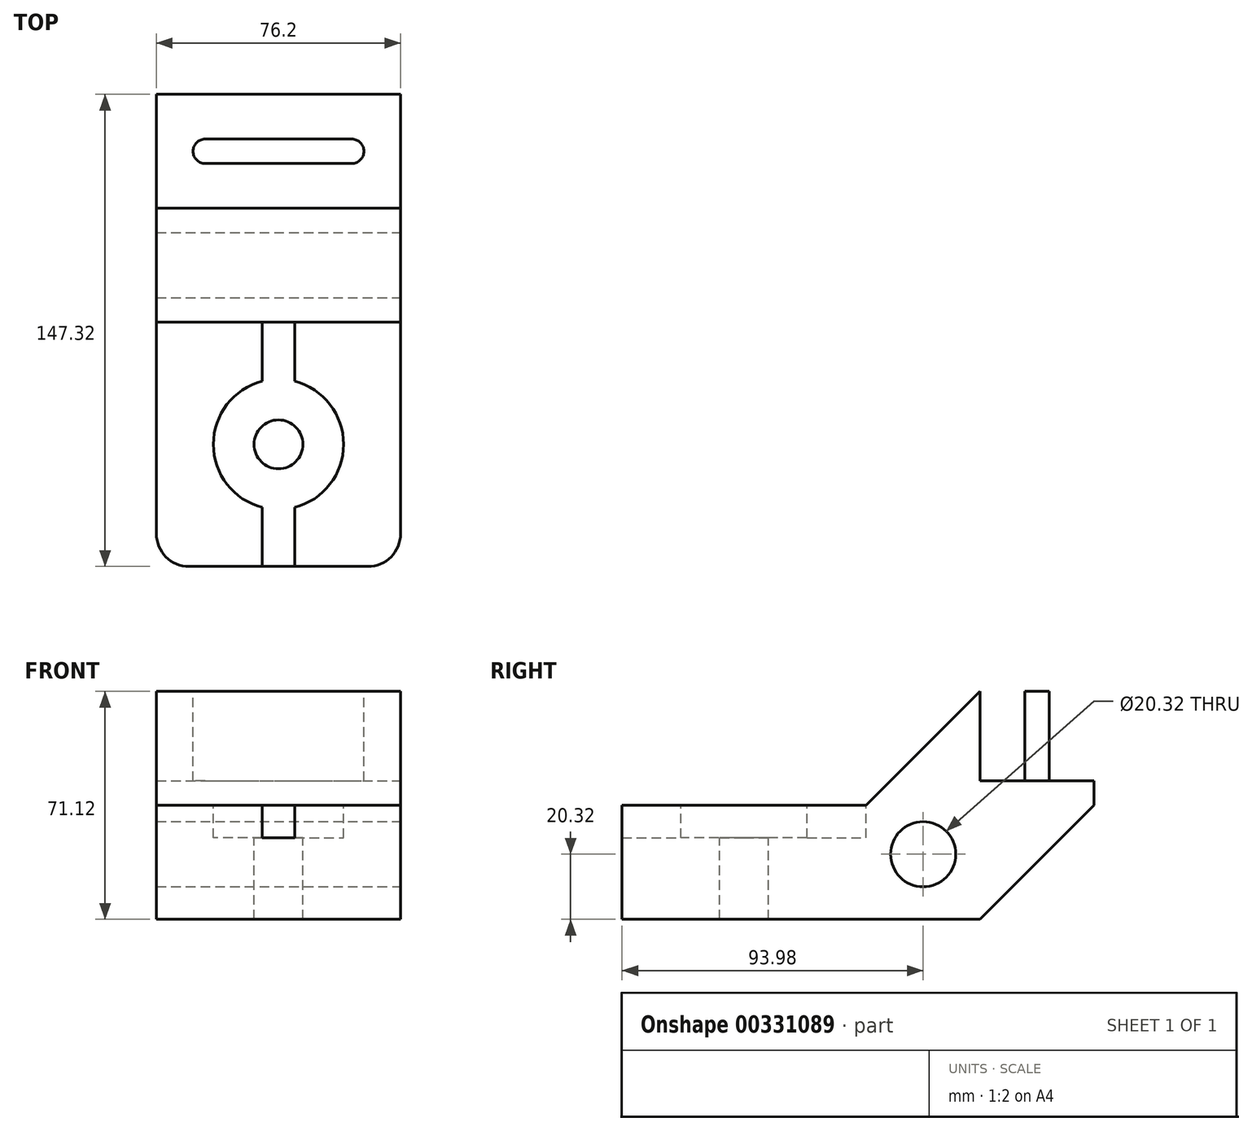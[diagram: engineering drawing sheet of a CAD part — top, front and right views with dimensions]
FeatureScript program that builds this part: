
annotation { "Feature Type Name" : "Feature", "Feature Type Description" : "" }
export const myFeature = defineFeature(function(context is Context, id is Id, definition is map)
    precondition{}
    {
        {
            var Q0;
            Q0=qCreatedBy(makeId("Top.planeOp"),FACE);
            var sketch = newSketch(context, id + "F0", { "sketchPlane" : qUnion([Q0])});
            skLineSegment(sketch, "E0.bottom", {"start": v(0, 0) * mm, "end": v(76.2, 0) * mm});
            skLineSegment(sketch, "E0.top", {"start": v(0, 147.32) * mm, "end": v(76.2, 147.32) * mm});
            skLineSegment(sketch, "E0.left", {"start": v(0, 0) * mm, "end": v(0, 147.32) * mm});
            skLineSegment(sketch, "E0.right", {"start": v(76.2, 0) * mm, "end": v(76.2, 147.32) * mm});
            skSolve(sketch);
        }
        {
            var Q0;
            Q0 = qSketchRegion(id + "F0", true);
            extrude(context, id + "F1", {"entities" : qUnion([Q0]), "depth" : 71.12 * mm});
        }
        {
            var Q0;
            Q0=makeQuery(id+"F1.opExtrude","SWEPT_FACE",FACE,{"disambiguationData":[OSD([sQuery(id+"F0.wireOp",EDGE,"E0.right")])]});
            var sketch = newSketch(context, id + "F2", { "sketchPlane" : qUnion([Q0])});
            skLineSegment(sketch, "E1", {"start": v(111.76, 0) * mm, "end": v(147.32, 35.56) * mm});
            skLineSegment(sketch, "E2", {"start": v(0, 35.56) * mm, "end": v(76.2, 35.56) * mm});
            skLineSegment(sketch, "E3", {"start": v(147.32, 71.12) * mm, "end": v(111.76, 71.12) * mm});
            skLineSegment(sketch, "E4", {"start": v(76.2, 35.56) * mm, "end": v(111.76, 71.12) * mm});
            skCircle(sketch, "E5", {"center": v(93.98, 20.32) * mm, "radius": 10.16 * mm});
            skSolve(sketch);
        }
        {
            var Q0;
            {var subQ0=sQuery(id+"F2.wireOp",EDGE,"E2");Q0=makeQuery(id+"F2.imprint","IMPRINT",FACE,{"disambiguationData":[TD([[makeQuery(id+"F2.imprint","IMPRINT",EDGE,{"derivedFrom":subQ0}),1.0]])]});}
            var Q1;
            {var subQ0=sQuery(id+"F2.wireOp",EDGE,"E1");Q1=makeQuery(id+"F2.imprint","IMPRINT",FACE,{"disambiguationData":[TD([[makeQuery(id+"F2.imprint","IMPRINT",EDGE,{"derivedFrom":subQ0}),-1.0]])]});}
            extrude(context, id + "F3", {"entities" : qUnion([Q0, Q1]), "operationType" : NewBodyOperationType.REMOVE, "endBound" : BoundingType.THROUGH_ALL, "oppositeDirection" : true, "depth" : 25.4 * mm});
        }
        {
            var Q0;
            Q0=makeQuery(id+"F1.opExtrude","SWEPT_EDGE",EDGE,{"disambiguationData":[OSD([sQuery(id+"F0.wireOp",EDGE,"E0.bottom"),sQuery(id+"F0.wireOp",EDGE,"E0.right")])]});
            var Q1;
            Q1=makeQuery(id+"F1.opExtrude","SWEPT_EDGE",EDGE,{"disambiguationData":[OSD([sQuery(id+"F0.wireOp",EDGE,"E0.bottom"),sQuery(id+"F0.wireOp",EDGE,"E0.left")])]});
            fillet(context, id + "F4", {"entities" : qUnion([Q0, Q1]), "radius" : 10.16 * mm, "tangentPropagation" : true, "allowEdgeOverflow" : false});
        }
        {
            var Q0;
            Q0=makeQuery(id+"F1.opExtrude","CAP_FACE",FACE,{"disambiguationData":[OSD([sQuery(id+"F0.wireOp",EDGE,"E0.bottom"),sQuery(id+"F0.wireOp",EDGE,"E0.top"),sQuery(id+"F0.wireOp",EDGE,"E0.left"),sQuery(id+"F0.wireOp",EDGE,"E0.right")])],"isStart":false});
            var sketch = newSketch(context, id + "F5", { "sketchPlane" : qUnion([Q0])});
            skLineSegment(sketch, "E6", {"start": v(15.24, 129.54) * mm, "end": v(60.96, 129.54) * mm, "construction": true});
            skArc(sketch, "E7.0.startCap", {"start": v(15.24, 125.73) * mm, "mid": v(11.43, 129.54) * mm, "end": v(15.24, 133.35) * mm});
            skArc(sketch, "E7.0.endCap", {"start": v(60.96, 133.35) * mm, "mid": v(64.77, 129.54) * mm, "end": v(60.96, 125.73) * mm});
            skLineSegment(sketch, "E7.0.left", {"start": v(15.24, 133.35) * mm, "end": v(60.96, 133.35) * mm});
            skLineSegment(sketch, "E7.0.right", {"start": v(15.24, 125.73) * mm, "end": v(60.96, 125.73) * mm});
            skSolve(sketch);
        }
        {
            var Q0;
            Q0=makeQuery(id+"F2.imprint","IMPRINT",FACE,{"disambiguationData":[TD([[makeQuery(id+"F2.imprint","IMPRINT",EDGE,{"derivedFrom":sQuery(id+"F2.wireOp",EDGE,"E5")}),1.0]])]});
            var Q1;
            {var subQ0=sQuery(id+"F2.wireOp",EDGE,"E1");Q1=makeQuery(id+"F2.imprint","IMPRINT",FACE,{"disambiguationData":[TD([[makeQuery(id+"F2.imprint","IMPRINT",EDGE,{"derivedFrom":subQ0}),-1.0]])]});}
            var Q2;
            {var subQ0=sQuery(id+"F2.wireOp",EDGE,"E2");Q2=makeQuery(id+"F2.imprint","IMPRINT",FACE,{"disambiguationData":[TD([[makeQuery(id+"F2.imprint","IMPRINT",EDGE,{"derivedFrom":subQ0}),1.0]])]});}
            extrude(context, id + "F6", {"entities" : qUnion([Q0, Q1, Q2]), "operationType" : NewBodyOperationType.REMOVE, "endBound" : BoundingType.THROUGH_ALL, "oppositeDirection" : true, "depth" : 25.4 * mm});
        }
        {
            var Q0;
            Q0=makeQuery(id+"F3.boolean.opBoolean","COPY",FACE,{"derivedFrom":makeQuery(id+"F3.opExtrude","SWEPT_FACE",FACE,{"disambiguationData":[OSD([sQuery(id+"F2.wireOp",EDGE,"E2")])]})});
            var sketch = newSketch(context, id + "F7", { "sketchPlane" : qUnion([Q0])});
            skPoint(sketch, "E8", {"position": v(38.1, 38.1) * mm});
            skLineSegment(sketch, "E9", {"start": v(33.02, 0) * mm, "end": v(33.02, 76.2) * mm});
            skLineSegment(sketch, "E10", {"start": v(43.18, 0) * mm, "end": v(43.18, 76.2) * mm});
            skLineSegment(sketch, "E11", {"start": v(38.1, -6.73) * mm, "end": v(38.1, 84.4) * mm, "construction": true});
            skPoint(sketch, "E11.startSnap0", {"position": v(38.1, 0) * mm});
            skPoint(sketch, "E11.endSnap0", {"position": v(38.1, 76.2) * mm});
            skLineSegment(sketch, "E12", {"start": v(33.02, 0) * mm, "end": v(43.18, 0) * mm});
            skLineSegment(sketch, "E13", {"start": v(33.02, 76.2) * mm, "end": v(43.18, 76.2) * mm});
            skSolve(sketch);
        }
        {
            var Q0;
            Q0=sQuery(id+"F7.wireOp",VERTEX,"E8");
            var Q1;
            Q1=makeQuery(id+"F1.opExtrude","SWEPT_BODY",BODY,{"disambiguationData":[OSD([sQuery(id+"F0.wireOp",EDGE,"E0.bottom"),sQuery(id+"F0.wireOp",EDGE,"E0.top"),sQuery(id+"F0.wireOp",EDGE,"E0.left"),sQuery(id+"F0.wireOp",EDGE,"E0.right")])]});
            hole(context, id + "F8", {"style" : HoleStyle.C_BORE, "endStyle" : HoleEndStyle.THROUGH, "holeDiameter" : 15.24 * mm, "cBoreDiameter" : 40.64 * mm, "cBoreDepth" : 10.16 * mm, "tappedDepth" : 12.7 * mm, "tapClearance" : 3, "locations" : qUnion([Q0]), "scope" : qUnion([Q1])});
        }
        {
            var Q0;
            Q0=makeQuery(id+"F5.imprint","IMPRINT",FACE,{"disambiguationData":[TD([[makeQuery(id+"F5.imprint","IMPRINT",EDGE,{"derivedFrom":sQuery(id+"F5.wireOp",EDGE,"E7.0.startCap")}),-1.0]])]});
            extrude(context, id + "F9", {"entities" : qUnion([Q0]), "operationType" : NewBodyOperationType.REMOVE, "oppositeDirection" : true, "depth" : 27.94 * mm});
        }
        {
            var Q0;
            Q0=makeQuery(id+"F7.imprint","IMPRINT",FACE,{"disambiguationData":[TD([[makeQuery(id+"F7.imprint","IMPRINT",EDGE,{"derivedFrom":sQuery(id+"F7.wireOp",EDGE,"E9")}),-1.0]])]});
            extrude(context, id + "F10", {"entities" : qUnion([Q0]), "operationType" : NewBodyOperationType.REMOVE, "oppositeDirection" : true, "depth" : 10.16 * mm});
        }
    });
